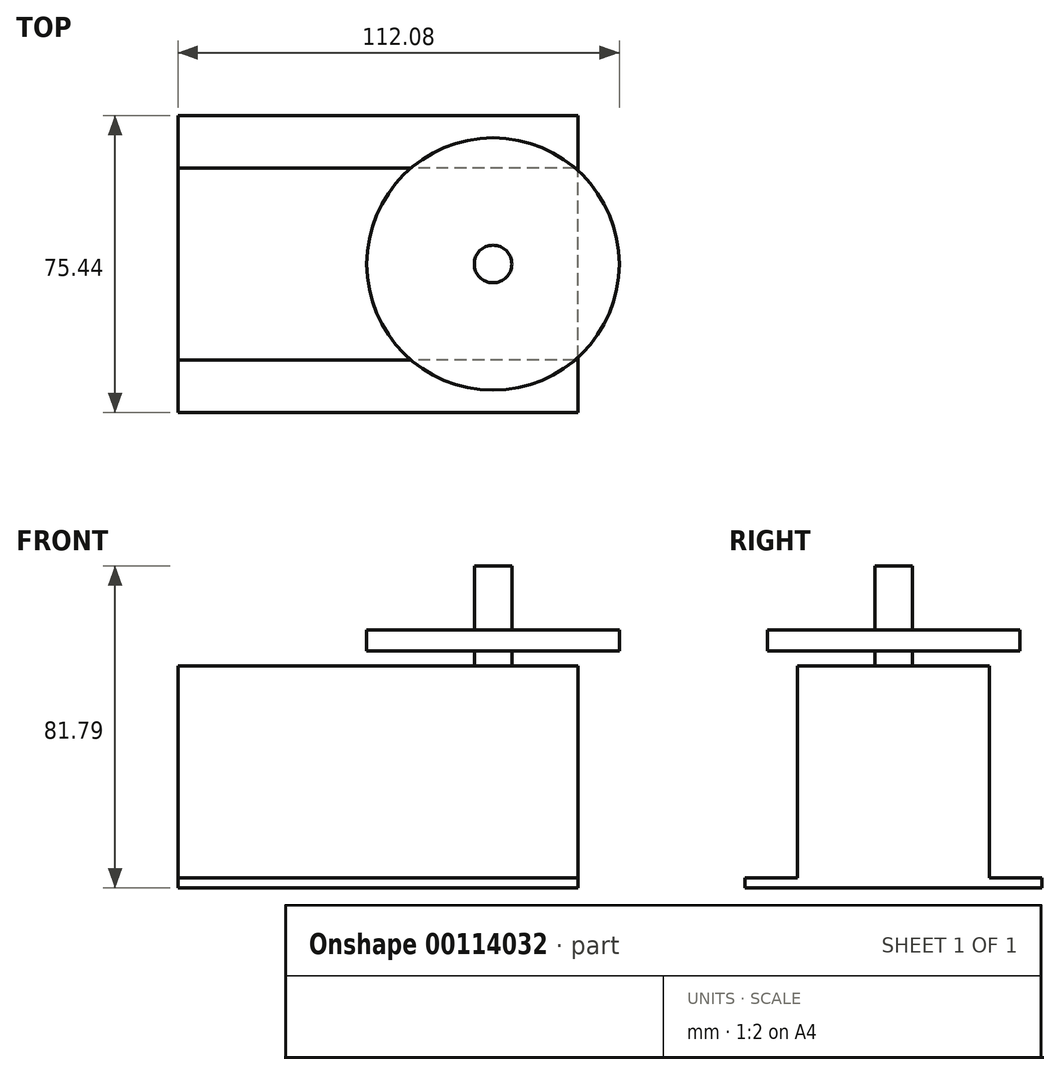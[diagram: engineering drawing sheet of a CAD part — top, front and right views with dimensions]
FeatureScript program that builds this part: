
annotation { "Feature Type Name" : "Feature", "Feature Type Description" : "" }
export const myFeature = defineFeature(function(context is Context, id is Id, definition is map)
    precondition{}
    {
        {
            var Q0;
            Q0=qCreatedBy(makeId("Top.planeOp"),FACE);
            var sketch = newSketch(context, id + "F0", { "sketchPlane" : qUnion([Q0])});
            skLineSegment(sketch, "E0.bottom", {"start": v(50.8, -37.72) * mm, "end": v(-50.8, -37.72) * mm});
            skLineSegment(sketch, "E0.top", {"start": v(50.8, 37.72) * mm, "end": v(-50.8, 37.72) * mm});
            skLineSegment(sketch, "E0.left", {"start": v(50.8, -37.72) * mm, "end": v(50.8, 37.72) * mm});
            skLineSegment(sketch, "E0.right", {"start": v(-50.8, -37.72) * mm, "end": v(-50.8, 37.72) * mm});
            skPoint(sketch, "E0.middle", {"position": v(0, 0) * mm});
            skLineSegment(sketch, "E1.bottom", {"start": v(50.8, -24.38) * mm, "end": v(-50.8, -24.38) * mm});
            skLineSegment(sketch, "E1.top", {"start": v(50.8, 24.38) * mm, "end": v(-50.8, 24.38) * mm});
            skLineSegment(sketch, "E1.left", {"start": v(50.8, -24.38) * mm, "end": v(50.8, 24.38) * mm});
            skLineSegment(sketch, "E1.right", {"start": v(-50.8, -24.38) * mm, "end": v(-50.8, 24.38) * mm});
            skSolve(sketch);
        }
        {
            var Q0;
            Q0=makeQuery(id+"F0.imprint","IMPRINT",FACE,{"disambiguationData":[TD([[makeQuery(id+"F0.imprint","IMPRINT",EDGE,{"derivedFrom":sQuery(id+"F0.wireOp",EDGE,"E1.bottom")}),-1.0]])]});
            extrude(context, id + "F1", {"entities" : qUnion([Q0]), "depth" : 56.4 * mm});
        }
        {
            var Q0;
            {var subQ0=sQuery(id+"F0.wireOp",EDGE,"E0.top");Q0=makeQuery(id+"F0.imprint","IMPRINT",FACE,{"disambiguationData":[TD([[makeQuery(id+"F0.imprint","IMPRINT",EDGE,{"derivedFrom":subQ0}),1.0]])]});}
            var Q1;
            {var subQ0=sQuery(id+"F0.wireOp",EDGE,"E0.bottom");Q1=makeQuery(id+"F0.imprint","IMPRINT",FACE,{"disambiguationData":[TD([[makeQuery(id+"F0.imprint","IMPRINT",EDGE,{"derivedFrom":subQ0}),-1.0]])]});}
            extrude(context, id + "F2", {"entities" : qUnion([Q0, Q1]), "operationType" : NewBodyOperationType.ADD, "depth" : 2.54 * mm});
        }
        {
            var Q0;
            Q0=makeQuery(id+"F1.opExtrude","CAP_FACE",FACE,{"disambiguationData":[OSD([sQuery(id+"F0.wireOp",EDGE,"E1.bottom"),sQuery(id+"F0.wireOp",EDGE,"E1.top"),sQuery(id+"F0.wireOp",EDGE,"E1.left"),sQuery(id+"F0.wireOp",EDGE,"E1.right")])],"isStart":false});
            var sketch = newSketch(context, id + "F3", { "sketchPlane" : qUnion([Q0])});
            skCircle(sketch, "E2", {"center": v(29.21, 0) * mm, "radius": 4.76 * mm});
            skPoint(sketch, "E2.centerSnap0", {"position": v(50.8, 0) * mm});
            skCircle(sketch, "E3", {"center": v(29.21, 0) * mm, "radius": 32.07 * mm});
            skSolve(sketch);
        }
        {
            var Q0;
            Q0=makeQuery(id+"F3.imprint","IMPRINT",FACE,{"disambiguationData":[TD([[makeQuery(id+"F3.imprint","IMPRINT",EDGE,{"derivedFrom":sQuery(id+"F3.wireOp",EDGE,"E2")}),1.0]])]});
            extrude(context, id + "F4", {"entities" : qUnion([Q0]), "operationType" : NewBodyOperationType.ADD, "depth" : 25.4 * mm});
        }
        {
            var Q0;
            Q0 = qSketchRegion(id + "F3", true);
            extrude(context, id + "F5", {"entities" : qUnion([Q0]), "operationType" : NewBodyOperationType.ADD, "depth" : 9.14 * mm});
        }
        {
            var Q0;
            Q0 = qSketchRegion(id + "F3", true);
            extrude(context, id + "F6", {"entities" : qUnion([Q0]), "operationType" : NewBodyOperationType.REMOVE, "depth" : 3.8 * mm});
        }
    });
